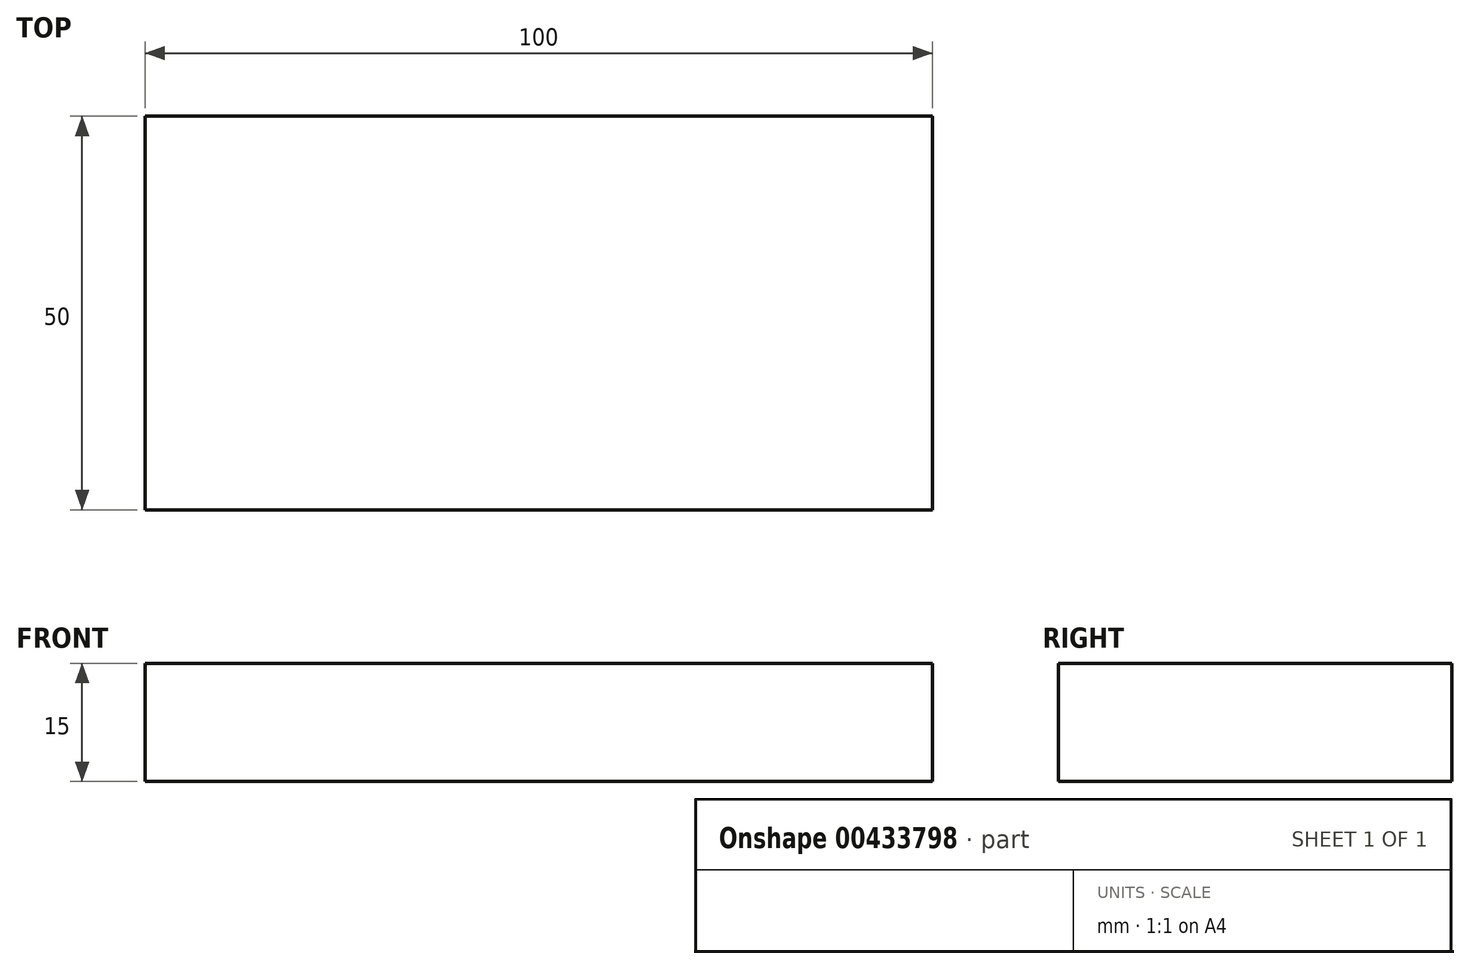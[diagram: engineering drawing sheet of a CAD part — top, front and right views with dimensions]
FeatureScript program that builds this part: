
annotation { "Feature Type Name" : "Feature", "Feature Type Description" : "" }
export const myFeature = defineFeature(function(context is Context, id is Id, definition is map)
    precondition{}
    {
        {
            var Q0;
            Q0=qCreatedBy(makeId("Top.planeOp"),FACE);
            var sketch = newSketch(context, id + "F0", { "sketchPlane" : qUnion([Q0])});
            skLineSegment(sketch, "E0.bottom", {"start": v(-52.22, 54.73) * mm, "end": v(47.78, 54.73) * mm});
            skLineSegment(sketch, "E0.top", {"start": v(-52.22, 4.73) * mm, "end": v(47.78, 4.73) * mm});
            skLineSegment(sketch, "E0.left", {"start": v(-52.22, 54.73) * mm, "end": v(-52.22, 4.73) * mm});
            skLineSegment(sketch, "E0.right", {"start": v(47.78, 54.73) * mm, "end": v(47.78, 4.73) * mm});
            skSolve(sketch);
        }
        {
            var Q0;
            Q0 = qSketchRegion(id + "F0", true);
            extrude(context, id + "F1", {"entities" : qUnion([Q0]), "depth" : 15 * mm});
        }
    });
